# Revit family: Robe_Hook-Surface_Mounted-Bobrick-B-7671X_Series
name_source: partatom
category: Specialty Equipment
units: mm (PartAtom-declared; Revit-internal decimal feet)

## family parameters
Cut with Voids When Loaded = No
Host = Face
OmniClass Number = 23.40.20.21.31
OmniClass Title = Robe Hooks
Part Type = Normal
Room Calculation Point = No
Round Connector Dimension = Use Diameter
Shared = Yes

## types (3) — shared parameters
ADA Compliant = Yes
Assembly Code = E2010
Default Elevation = 40"
Description = Surface-Mounted Robe Hook
Height = 2"
Installation Type = Surface-Mounted
Length = 2"
Manufacturer = Bobrick
Mounting Height = 38"
Mounting Height Constraint = 38"
Product Documentation Link = https://www.bobrick.com
Product Page URL = https://www.bobrick.com
Revised Date = 05/07/2025
URL = http://www.bobrick.com
Warranty Documentation Link = https://www.bobrick.com
Width = 1 5/8"

## per-type parameters (varying)
| type | Finish | Material | Model |
| B-7671 | Stainless Steel-Bobrick-Bright Polished | Stainless Steel-Bobrick-Bright Polished | B-7671 |
| B-76717 | Stainless Steel-Bobrick-Satin | Stainless Steel-Bobrick-Satin | B-7671 |
| B-7671.MBLK | Stainless Steel-Bobrick-Matte Black | Stainless Steel-Bobrick-Matte Black | B-7671.MBLK |

## geometry (parser evidence)
native form markers: Sweep x3
no freeform markers — native parametric forms only
